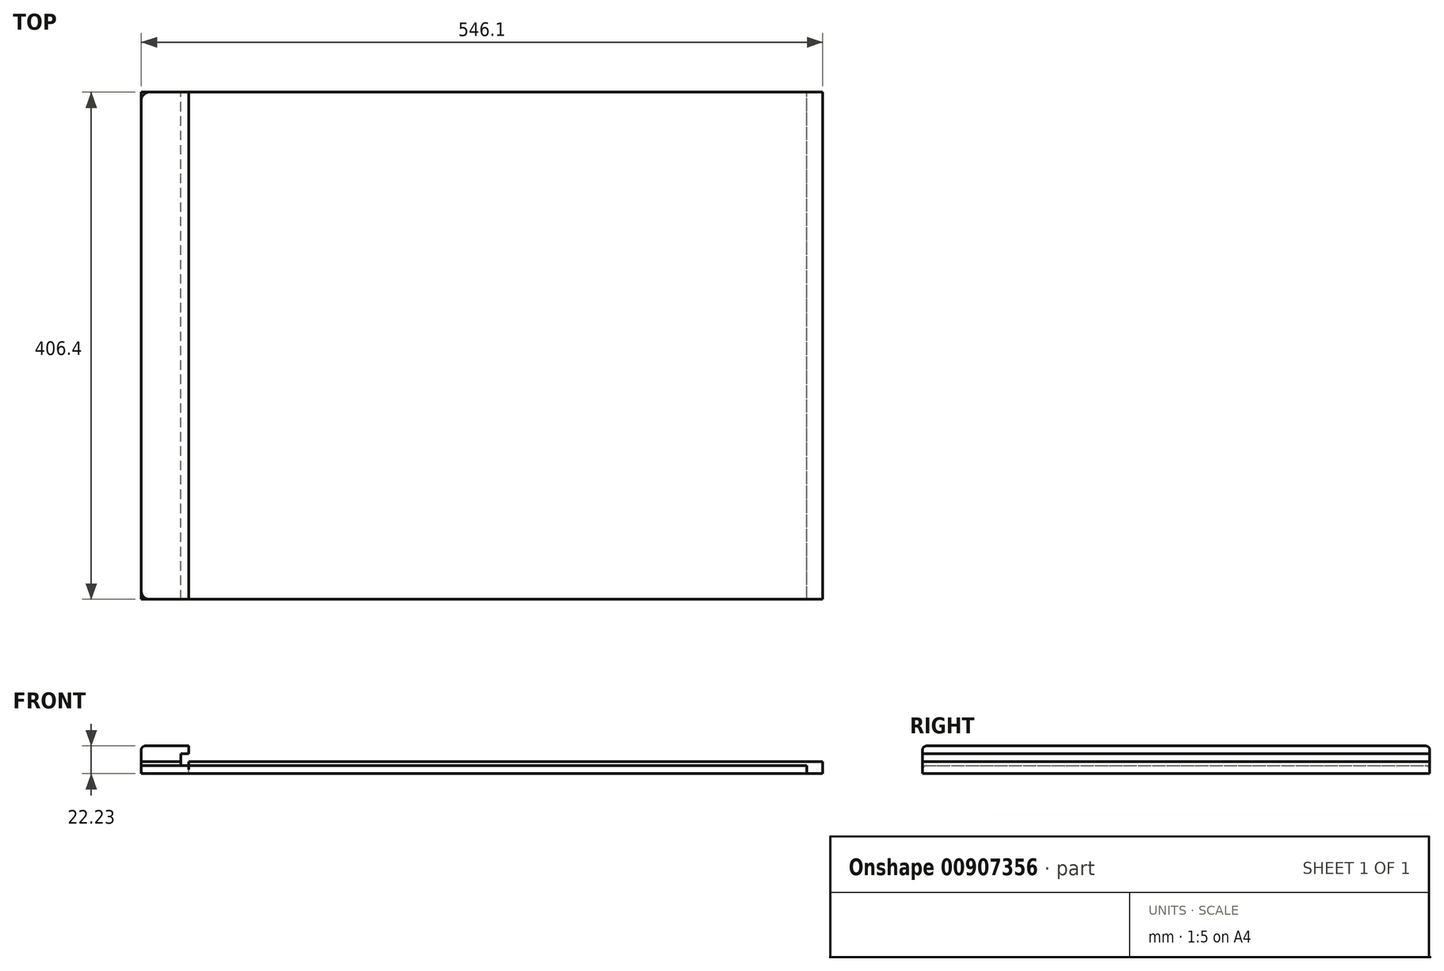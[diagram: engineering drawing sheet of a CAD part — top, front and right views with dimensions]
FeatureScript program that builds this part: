
annotation { "Feature Type Name" : "Feature", "Feature Type Description" : "" }
export const myFeature = defineFeature(function(context is Context, id is Id, definition is map)
    precondition{}
    {
        {
            var Q0;
            Q0=qCreatedBy(makeId("Top.planeOp"),FACE);
            var sketch = newSketch(context, id + "F0", { "sketchPlane" : qUnion([Q0])});
            skLineSegment(sketch, "E0.bottom", {"start": v(0, 0) * mm, "end": v(546.1, 0) * mm});
            skLineSegment(sketch, "E0.top", {"start": v(0, 406.4) * mm, "end": v(546.1, 406.4) * mm});
            skLineSegment(sketch, "E0.left", {"start": v(0, 0) * mm, "end": v(0, 406.4) * mm});
            skLineSegment(sketch, "E0.right", {"start": v(546.1, 0) * mm, "end": v(546.1, 406.4) * mm});
            skSolve(sketch);
        }
        {
            var Q0;
            Q0=makeQuery(id+"F0.imprint","IMPRINT",FACE,{"disambiguationData":[TD([[makeQuery(id+"F0.imprint","IMPRINT",EDGE,{"derivedFrom":sQuery(id+"F0.wireOp",EDGE,"E0.bottom")}),1.0]])]});
            extrude(context, id + "F1", {"entities" : qUnion([Q0]), "depth" : 9.52 * mm, "offsetDistance" : 25.4 * mm});
        }
        {
            var Q0;
            Q0=qCreatedBy(makeId("Top.planeOp"),FACE);
            var sketch = newSketch(context, id + "F2", { "sketchPlane" : qUnion([Q0])});
            skLineSegment(sketch, "E1.bottom", {"start": v(0, 0) * mm, "end": v(533.4, 0) * mm});
            skLineSegment(sketch, "E1.top", {"start": v(0, 406.4) * mm, "end": v(533.4, 406.4) * mm});
            skLineSegment(sketch, "E1.left", {"start": v(0, 0) * mm, "end": v(0, 406.4) * mm});
            skLineSegment(sketch, "E1.right", {"start": v(533.4, 0) * mm, "end": v(533.4, 406.4) * mm});
            skSolve(sketch);
        }
        {
            var Q0;
            Q0=makeQuery(id+"F2.imprint","IMPRINT",FACE,{"disambiguationData":[TD([[makeQuery(id+"F2.imprint","IMPRINT",EDGE,{"derivedFrom":sQuery(id+"F2.wireOp",EDGE,"E1.bottom")}),1.0]])]});
            extrude(context, id + "F3", {"entities" : qUnion([Q0]), "depth" : 6.35 * mm, "offsetDistance" : 25.4 * mm});
        }
        {
            var Q0;
            Q0=makeQuery(id+"F3.opExtrude","CAP_EDGE",EDGE,{"disambiguationData":[OSD([sQuery(id+"F2.wireOp",EDGE,"E1.bottom")])],"isStart":false});
            var Q1;
            Q1=makeQuery(id+"F3.opExtrude","CAP_EDGE",EDGE,{"disambiguationData":[OSD([sQuery(id+"F2.wireOp",EDGE,"E1.top")])],"isStart":false});
            fillet(context, id + "F4", {"entities" : qUnion([Q0, Q1]), "radius" : 3.17 * mm, "tangentPropagation" : true, "allowEdgeOverflow" : false});
        }
        {
            var Q0;
            Q0=qCreatedBy(makeId("Top.planeOp"),FACE);
            var sketch = newSketch(context, id + "F5", { "sketchPlane" : qUnion([Q0])});
            skLineSegment(sketch, "E2.bottom", {"start": v(0, 0) * mm, "end": v(533.4, 0) * mm});
            skLineSegment(sketch, "E2.top", {"start": v(0, 406.4) * mm, "end": v(533.4, 406.4) * mm});
            skLineSegment(sketch, "E2.left", {"start": v(0, 0) * mm, "end": v(0, 406.4) * mm});
            skLineSegment(sketch, "E2.right", {"start": v(533.4, 0) * mm, "end": v(533.4, 406.4) * mm});
            skSolve(sketch);
        }
        {
            var Q0;
            Q0=makeQuery(id+"F5.imprint","IMPRINT",FACE,{"disambiguationData":[TD([[makeQuery(id+"F5.imprint","IMPRINT",EDGE,{"derivedFrom":sQuery(id+"F5.wireOp",EDGE,"E2.bottom")}),1.0]])]});
            extrude(context, id + "F6", {"entities" : qUnion([Q0]), "depth" : 6.35 * mm, "offsetDistance" : 25.4 * mm});
        }
        {
            var Q0;
            Q0=makeQuery(id+"F6.opExtrude","CAP_EDGE",EDGE,{"disambiguationData":[OSD([sQuery(id+"F5.wireOp",EDGE,"E2.bottom")])],"isStart":true});
            var Q1;
            Q1=makeQuery(id+"F6.opExtrude","CAP_EDGE",EDGE,{"disambiguationData":[OSD([sQuery(id+"F5.wireOp",EDGE,"E2.top")])],"isStart":true});
            fillet(context, id + "F7", {"entities" : qUnion([Q0, Q1]), "radius" : 3.17 * mm, "tangentPropagation" : true, "allowEdgeOverflow" : false});
        }
        {
            var Q0;
            Q0=qCreatedBy(makeId("Top.planeOp"),FACE);
            var sketch = newSketch(context, id + "F8", { "sketchPlane" : qUnion([Q0])});
            skLineSegment(sketch, "E3.bottom", {"start": v(0, 0) * mm, "end": v(38.1, 0) * mm});
            skLineSegment(sketch, "E3.top", {"start": v(0, 406.4) * mm, "end": v(38.1, 406.4) * mm});
            skLineSegment(sketch, "E3.left", {"start": v(0, 0) * mm, "end": v(0, 406.4) * mm});
            skLineSegment(sketch, "E3.right", {"start": v(38.1, 0) * mm, "end": v(38.1, 406.4) * mm});
            skSolve(sketch);
        }
        {
            var Q0;
            Q0=makeQuery(id+"F8.imprint","IMPRINT",FACE,{"disambiguationData":[TD([[makeQuery(id+"F8.imprint","IMPRINT",EDGE,{"derivedFrom":sQuery(id+"F8.wireOp",EDGE,"E3.bottom")}),1.0]])]});
            extrude(context, id + "F9", {"entities" : qUnion([Q0]), "depth" : 22.22 * mm, "offsetDistance" : 25.4 * mm});
        }
        {
            var Q0;
            Q0=makeQuery(id+"F9.opExtrude","SWEPT_FACE",FACE,{"disambiguationData":[OSD([sQuery(id+"F8.wireOp",EDGE,"E3.right")])]});
            var sketch = newSketch(context, id + "F10", { "sketchPlane" : qUnion([Q0])});
            skLineSegment(sketch, "E4.bottom", {"start": v(0, 15.88) * mm, "end": v(406.4, 15.88) * mm});
            skLineSegment(sketch, "E4.top", {"start": v(0, 6.35) * mm, "end": v(406.4, 6.35) * mm});
            skLineSegment(sketch, "E4.left", {"start": v(0, 15.88) * mm, "end": v(0, 6.35) * mm});
            skLineSegment(sketch, "E4.right", {"start": v(406.4, 15.88) * mm, "end": v(406.4, 6.35) * mm});
            skSolve(sketch);
        }
        {
            var Q0;
            Q0=makeQuery(id+"F10.imprint","IMPRINT",FACE,{"disambiguationData":[TD([[makeQuery(id+"F10.imprint","IMPRINT",EDGE,{"derivedFrom":sQuery(id+"F10.wireOp",EDGE,"E4.bottom")}),-1.0]])]});
            extrude(context, id + "F11", {"entities" : qUnion([Q0]), "operationType" : NewBodyOperationType.REMOVE, "oppositeDirection" : true, "depth" : 6.35 * mm, "offsetDistance" : 25.4 * mm});
        }
        {
            var Q0;
            Q0=makeQuery(id+"F9.opExtrude","SWEPT_EDGE",EDGE,{"disambiguationData":[OSD([sQuery(id+"F8.wireOp",EDGE,"E3.bottom"),sQuery(id+"F8.wireOp",EDGE,"E3.left")])]});
            var Q1;
            Q1=makeQuery(id+"F9.opExtrude","SWEPT_EDGE",EDGE,{"disambiguationData":[OSD([sQuery(id+"F8.wireOp",EDGE,"E3.top"),sQuery(id+"F8.wireOp",EDGE,"E3.left")])]});
            fillet(context, id + "F12", {"entities" : qUnion([Q0, Q1]), "radius" : 6.35 * mm, "tangentPropagation" : true, "allowEdgeOverflow" : false});
        }
        {
            var Q0;
            Q0=makeQuery(id+"F9.opExtrude","CAP_EDGE",EDGE,{"disambiguationData":[OSD([sQuery(id+"F8.wireOp",EDGE,"E3.top")])],"isStart":true});
            var Q1;
            {var subQ0=sQuery(id+"F8.wireOp",EDGE,"E3.left");var subQ1=sQuery(id+"F8.wireOp",EDGE,"E3.top");Q1=makeQuery(id+"F12.opFillet","BLEND_EDGE",EDGE,{"blendedFrom":[makeQuery(id+"F9.opExtrude","SWEPT_EDGE",EDGE,{"disambiguationData":[OSD([subQ1,subQ0])]}),makeQuery(id+"F9.opExtrude","CAP_FACE",FACE,{"disambiguationData":[OSD([sQuery(id+"F8.wireOp",EDGE,"E3.bottom"),subQ1,subQ0,sQuery(id+"F8.wireOp",EDGE,"E3.right")])],"isStart":true})],"blendedInto":[makeQuery(id+"F9.opExtrude","CAP_FACE",FACE,{"disambiguationData":[OSD([sQuery(id+"F8.wireOp",EDGE,"E3.bottom"),subQ1,subQ0,sQuery(id+"F8.wireOp",EDGE,"E3.right")])],"isStart":true})]});}
            var Q2;
            Q2=makeQuery(id+"F9.opExtrude","CAP_EDGE",EDGE,{"disambiguationData":[OSD([sQuery(id+"F8.wireOp",EDGE,"E3.left")])],"isStart":true});
            var Q3;
            {var subQ0=sQuery(id+"F8.wireOp",EDGE,"E3.left");var subQ1=sQuery(id+"F8.wireOp",EDGE,"E3.bottom");Q3=makeQuery(id+"F12.opFillet","BLEND_EDGE",EDGE,{"blendedFrom":[makeQuery(id+"F9.opExtrude","SWEPT_EDGE",EDGE,{"disambiguationData":[OSD([subQ1,subQ0])]}),makeQuery(id+"F9.opExtrude","CAP_FACE",FACE,{"disambiguationData":[OSD([subQ1,sQuery(id+"F8.wireOp",EDGE,"E3.top"),subQ0,sQuery(id+"F8.wireOp",EDGE,"E3.right")])],"isStart":true})],"blendedInto":[makeQuery(id+"F9.opExtrude","CAP_FACE",FACE,{"disambiguationData":[OSD([subQ1,sQuery(id+"F8.wireOp",EDGE,"E3.top"),subQ0,sQuery(id+"F8.wireOp",EDGE,"E3.right")])],"isStart":true})]});}
            var Q4;
            Q4=makeQuery(id+"F9.opExtrude","CAP_EDGE",EDGE,{"disambiguationData":[OSD([sQuery(id+"F8.wireOp",EDGE,"E3.bottom")])],"isStart":true});
            fillet(context, id + "F13", {"entities" : qUnion([Q0, Q1, Q2, Q3, Q4]), "radius" : 3.17 * mm, "tangentPropagation" : true, "allowEdgeOverflow" : false});
        }
        {
            var Q0;
            Q0=makeQuery(id+"F9.opExtrude","CAP_EDGE",EDGE,{"disambiguationData":[OSD([sQuery(id+"F8.wireOp",EDGE,"E3.bottom")])],"isStart":false});
            var Q1;
            {var subQ0=sQuery(id+"F8.wireOp",EDGE,"E3.left");var subQ1=sQuery(id+"F8.wireOp",EDGE,"E3.bottom");Q1=makeQuery(id+"F12.opFillet","BLEND_EDGE",EDGE,{"blendedFrom":[makeQuery(id+"F9.opExtrude","SWEPT_EDGE",EDGE,{"disambiguationData":[OSD([subQ1,subQ0])]}),makeQuery(id+"F9.opExtrude","CAP_FACE",FACE,{"disambiguationData":[OSD([subQ1,sQuery(id+"F8.wireOp",EDGE,"E3.top"),subQ0,sQuery(id+"F8.wireOp",EDGE,"E3.right")])],"isStart":false})],"blendedInto":[makeQuery(id+"F9.opExtrude","CAP_FACE",FACE,{"disambiguationData":[OSD([subQ1,sQuery(id+"F8.wireOp",EDGE,"E3.top"),subQ0,sQuery(id+"F8.wireOp",EDGE,"E3.right")])],"isStart":false})]});}
            var Q2;
            Q2=makeQuery(id+"F9.opExtrude","CAP_EDGE",EDGE,{"disambiguationData":[OSD([sQuery(id+"F8.wireOp",EDGE,"E3.left")])],"isStart":false});
            var Q3;
            {var subQ0=sQuery(id+"F8.wireOp",EDGE,"E3.left");var subQ1=sQuery(id+"F8.wireOp",EDGE,"E3.top");Q3=makeQuery(id+"F12.opFillet","BLEND_EDGE",EDGE,{"blendedFrom":[makeQuery(id+"F9.opExtrude","SWEPT_EDGE",EDGE,{"disambiguationData":[OSD([subQ1,subQ0])]}),makeQuery(id+"F9.opExtrude","CAP_FACE",FACE,{"disambiguationData":[OSD([sQuery(id+"F8.wireOp",EDGE,"E3.bottom"),subQ1,subQ0,sQuery(id+"F8.wireOp",EDGE,"E3.right")])],"isStart":false})],"blendedInto":[makeQuery(id+"F9.opExtrude","CAP_FACE",FACE,{"disambiguationData":[OSD([sQuery(id+"F8.wireOp",EDGE,"E3.bottom"),subQ1,subQ0,sQuery(id+"F8.wireOp",EDGE,"E3.right")])],"isStart":false})]});}
            var Q4;
            Q4=makeQuery(id+"F9.opExtrude","CAP_EDGE",EDGE,{"disambiguationData":[OSD([sQuery(id+"F8.wireOp",EDGE,"E3.top")])],"isStart":false});
            fillet(context, id + "F14", {"entities" : qUnion([Q0, Q1, Q2, Q3, Q4]), "radius" : 3.17 * mm, "tangentPropagation" : true, "allowEdgeOverflow" : false});
        }
    });
